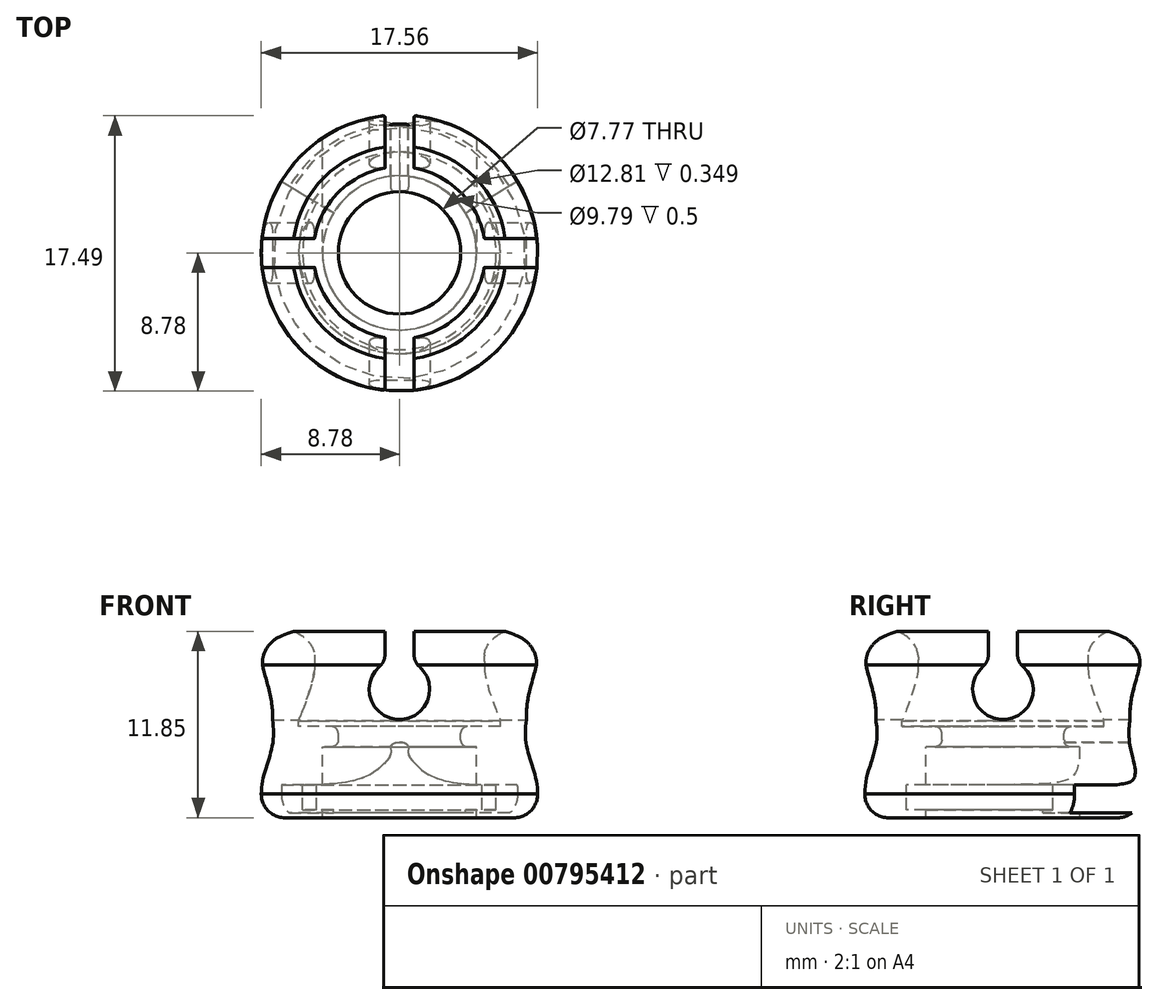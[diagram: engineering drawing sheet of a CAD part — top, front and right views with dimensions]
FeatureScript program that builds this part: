
annotation { "Feature Type Name" : "Feature", "Feature Type Description" : "" }
export const myFeature = defineFeature(function(context is Context, id is Id, definition is map)
    precondition{}
    {
        {
            var Q0;
            Q0=qCreatedBy(makeId("Front.planeOp"),FACE);
            var sketch = newSketch(context, id + "F0", { "sketchPlane" : qUnion([Q0])});
            skLineSegment(sketch, "E0", {"start": v(-3.88, 3.25) * mm, "end": v(-3.88, 2.85) * mm});
            skLineSegment(sketch, "E1", {"start": v(-4.34, 2.4) * mm, "end": v(-4.9, 2.4) * mm});
            skLineSegment(sketch, "E2", {"start": v(-4.9, 2.4) * mm, "end": v(-4.9, 0) * mm});
            skLineSegment(sketch, "E3", {"start": v(-4.9, 0) * mm, "end": v(-6.14, 0) * mm});
            skLineSegment(sketch, "E4", {"start": v(-6.14, 0) * mm, "end": v(-6.14, -1.6) * mm});
            skLineSegment(sketch, "E5", {"start": v(-6.14, -1.6) * mm, "end": v(-4.9, -1.6) * mm});
            skLineSegment(sketch, "E6", {"start": v(-4.9, -1.6) * mm, "end": v(-4.9, -2.1) * mm});
            skLineSegment(sketch, "E7", {"start": v(-4.9, -2.1) * mm, "end": v(-7.28, -2.1) * mm});
            skLineSegment(sketch, "E8", {"start": v(-8.78, -0.6) * mm, "end": v(-8.78, -0.6) * mm});
            skLineSegment(sketch, "E9", {"start": v(-7.47, 9.5) * mm, "end": v(-6.77, 9.75) * mm});
            skLineSegment(sketch, "E10", {"start": v(0, 14.29) * mm, "end": v(0, -15.3) * mm, "construction": true});
            skLineSegment(sketch, "E11", {"start": v(-6.4, 4.05) * mm, "end": v(-6.4, 3.7) * mm});
            skLineSegment(sketch, "E12", {"start": v(-6.4, 3.7) * mm, "end": v(-4.34, 3.7) * mm});
            skPoint(sketch, "E13.visualSharp", {"position": v(-8.78, 9) * mm});
            skArc(sketch, "E13.filletArc", {"start": v(-7.47, 9.5) * mm, "mid": v(-8.42, 8.76) * mm, "end": v(-8.78, 7.62) * mm});
            skPoint(sketch, "E14.visualSharp", {"position": v(-8.78, -2.1) * mm});
            skArc(sketch, "E14.filletArc", {"start": v(-8.78, -0.6) * mm, "mid": v(-8.34, -1.66) * mm, "end": v(-7.28, -2.1) * mm});
            skFitSpline(sketch, "E15", {"points": [v(-8.77, 7.62) * mm, v(-8, 3.1) * mm, v(-8.77, -0.6) * mm], "startDerivative": vector(0.2, -7.43) * mm, "endDerivative": vector(0.17, -8.43) * mm});
            skPoint(sketch, "E16.2.internal.snap0", {"position": v(-5.95, 7.8) * mm});
            skFitSpline(sketch, "E16", {"points": [v(-6.77, 9.75) * mm, v(-5.5, 8.43) * mm, v(-5.95, 6.2) * mm, v(-6.4, 4.05) * mm], "startDerivative": vector(5.68, -2.33) * mm, "endDerivative": vector(-0.9, -5.9) * mm});
            skPoint(sketch, "E17.orphan", {"position": v(-6.4, 7.18) * mm});
            skPoint(sketch, "E18.visualSharp", {"position": v(-3.88, 3.7) * mm});
            skArc(sketch, "E18.filletArc", {"start": v(-3.88, 3.25) * mm, "mid": v(-4.02, 3.57) * mm, "end": v(-4.34, 3.7) * mm});
            skPoint(sketch, "E19.visualSharp", {"position": v(-3.88, 2.4) * mm});
            skArc(sketch, "E19.filletArc", {"start": v(-4.34, 2.4) * mm, "mid": v(-4.02, 2.53) * mm, "end": v(-3.88, 2.85) * mm});
            skSolve(sketch);
        }
        {
            var Q0;
            Q0 = qSketchRegion(id + "F0", true);
            var Q1;
            Q1=sQuery(id+"F0.wireOp",EDGE,"E10");
            revolve(context, id + "F1", {"surfaceOperationType" : NewSurfaceOperationType.NEW, "entities" : qUnion([Q0]), "axis" : qUnion([Q1]), "revolveType" : RevolveType.FULL});
        }
        {
            var Q0;
            Q0=qCreatedBy(makeId("Right.planeOp"),FACE);
            var sketch = newSketch(context, id + "F2", { "sketchPlane" : qUnion([Q0])});
            skArc(sketch, "E20", {"start": v(-1.27, 7.5) * mm, "mid": v(0, 4.13) * mm, "end": v(1.27, 7.5) * mm});
            skLineSegment(sketch, "E21.top", {"start": v(-0.92, 15.11) * mm, "end": v(0.93, 15.11) * mm});
            skLineSegment(sketch, "E21.left", {"start": v(-0.92, 8.26) * mm, "end": v(-0.92, 15.11) * mm});
            skLineSegment(sketch, "E21.right", {"start": v(0.93, 8.26) * mm, "end": v(0.93, 15.11) * mm});
            skPoint(sketch, "E21.middle", {"position": v(0, 11.1) * mm});
            skPoint(sketch, "E22.orphan", {"position": v(0.93, 7.1) * mm});
            skPoint(sketch, "E23.orphan", {"position": v(-0.92, 7.1) * mm});
            skPoint(sketch, "E24.visualSharp", {"position": v(0.93, 7.74) * mm});
            skArc(sketch, "E24.filletArc", {"start": v(0.92, 8.26) * mm, "mid": v(1.01, 7.84) * mm, "end": v(1.27, 7.5) * mm});
            skPoint(sketch, "E25.visualSharp", {"position": v(-0.92, 7.74) * mm});
            skArc(sketch, "E25.filletArc", {"start": v(-1.27, 7.5) * mm, "mid": v(-1.01, 7.84) * mm, "end": v(-0.92, 8.26) * mm});
            skSolve(sketch);
        }
        {
            var Q0;
            Q0 = qSketchRegion(id + "F2", true);
            extrude(context, id + "F3", {"entities" : qUnion([Q0]), "operationType" : NewBodyOperationType.REMOVE, "endBound" : BoundingType.SYMMETRIC, "oppositeDirection" : true, "depth" : 25 * mm, "offsetDistance" : 25 * mm});
        }
        {
            var Q0;
            Q0=qCreatedBy(makeId("Front.planeOp"),FACE);
            var sketch = newSketch(context, id + "F4", { "sketchPlane" : qUnion([Q0])});
            skArc(sketch, "E26", {"start": v(-1.27, 7.5) * mm, "mid": v(0, 4.13) * mm, "end": v(1.27, 7.5) * mm});
            skLineSegment(sketch, "E27.top", {"start": v(-0.92, 15.11) * mm, "end": v(0.93, 15.11) * mm});
            skLineSegment(sketch, "E27.left", {"start": v(-0.92, 8.26) * mm, "end": v(-0.92, 15.11) * mm});
            skLineSegment(sketch, "E27.right", {"start": v(0.93, 8.26) * mm, "end": v(0.93, 15.11) * mm});
            skPoint(sketch, "E27.middle", {"position": v(0, 11.1) * mm});
            skPoint(sketch, "E28.orphan", {"position": v(0.93, 7.1) * mm});
            skPoint(sketch, "E29.orphan", {"position": v(-0.92, 7.1) * mm});
            skPoint(sketch, "E30.visualSharp", {"position": v(0.93, 7.74) * mm});
            skArc(sketch, "E30.filletArc", {"start": v(0.93, 8.26) * mm, "mid": v(1.01, 7.84) * mm, "end": v(1.27, 7.5) * mm});
            skPoint(sketch, "E31.visualSharp", {"position": v(-0.92, 7.74) * mm});
            skArc(sketch, "E31.filletArc", {"start": v(-1.27, 7.5) * mm, "mid": v(-1.01, 7.84) * mm, "end": v(-0.92, 8.26) * mm});
            skSolve(sketch);
        }
        {
            var Q0;
            Q0 = qSketchRegion(id + "F4", true);
            extrude(context, id + "F5", {"entities" : qUnion([Q0]), "operationType" : NewBodyOperationType.REMOVE, "endBound" : BoundingType.SYMMETRIC, "oppositeDirection" : true, "depth" : 25 * mm, "offsetDistance" : 25 * mm});
        }
        {
            var Q0;
            Q0=qCreatedBy(makeId("Front.planeOp"),FACE);
            var sketch = newSketch(context, id + "F6", { "sketchPlane" : qUnion([Q0])});
            skFitSpline(sketch, "E32", {"points": [v(-4.9, 0) * mm, v(-2.89, 0.26) * mm, v(-1.45, 0.92) * mm, v(-0.69, 1.68) * mm, v(-0.54, 2.03) * mm, v(0, 2.68) * mm], "startDerivative": vector(7.16, 0.52) * mm, "endDerivative": vector(12.5, -0.27) * mm});
            skLineSegment(sketch, "E33", {"start": v(-4.9, 0) * mm, "end": v(0, 0) * mm});
            skLineSegment(sketch, "E34", {"start": v(0, 5.3) * mm, "end": v(0, -2.76) * mm, "construction": true});
            skFitSpline(sketch, "E35.MirrorCS", {"points": [v(4.9, 0) * mm, v(2.89, 0.26) * mm, v(1.45, 0.92) * mm, v(0.69, 1.68) * mm, v(0.54, 2.03) * mm, v(0, 2.68) * mm], "startDerivative": vector(-7.16, 0.52) * mm, "endDerivative": vector(-12.5, -0.27) * mm});
            skLineSegment(sketch, "E36.MirrorCS", {"start": v(4.9, 0) * mm, "end": v(0, 0) * mm});
            skSolve(sketch);
        }
        {
            var Q0;
            Q0 = qSketchRegion(id + "F6", true);
            extrude(context, id + "F7", {"entities" : qUnion([Q0]), "operationType" : NewBodyOperationType.REMOVE, "oppositeDirection" : true, "depth" : 25 * mm, "offsetDistance" : 25 * mm});
        }
        {
            var Q0;
            Q0=makeQuery(id+"F7.boolean.opBoolean","COPY",FACE,{"derivedFrom":makeQuery(id+"F7.opExtrude","SWEPT_FACE",FACE,{"disambiguationData":[OSD([sQuery(id+"F6.wireOp",EDGE,"E33"),sQuery(id+"F6.wireOp",EDGE,"E36.MirrorCS")])]})});
            var sketch = newSketch(context, id + "F8", { "sketchPlane" : qUnion([Q0])});
            skLineSegment(sketch, "E37", {"start": v(-8.24, 5) * mm, "end": v(0, 0) * mm});
            skLineSegment(sketch, "E38", {"start": v(-8.24, 5) * mm, "end": v(0, 13.4) * mm});
            skLineSegment(sketch, "E39", {"start": v(0, 18.68) * mm, "end": v(0, -2.52) * mm, "construction": true});
            skLineSegment(sketch, "E40.MirrorCS", {"start": v(8.24, 5) * mm, "end": v(0, 13.4) * mm});
            skLineSegment(sketch, "E41.MirrorCS", {"start": v(8.24, 5) * mm, "end": v(0, 0) * mm});
            skSolve(sketch);
        }
        {
            var Q0;
            Q0 = qSketchRegion(id + "F8", true);
            extrude(context, id + "F9", {"entities" : qUnion([Q0]), "operationType" : NewBodyOperationType.REMOVE, "oppositeDirection" : true, "depth" : 1.8 * mm, "offsetDistance" : 25 * mm});
        }
    });
